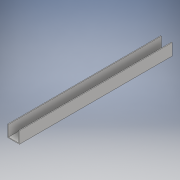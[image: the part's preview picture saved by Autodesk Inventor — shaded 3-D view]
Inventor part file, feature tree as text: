
AUTODESK INVENTOR PART (.ipt)
format: ipt  version: 2017 (Build 210142000, 142)  size: 100,352 bytes
history: native  units: in
note: dims shown in document units (in); Inventor stores cm internally (conversion verified against a paired STEP export)
features: sketch x2, extrude x1
ambient origin geometry x8: Origin, YZ Plane, XZ Plane, XY Plane, X Axis, Y Axis, Z Axis, Center Point
bodies: Solid1 (feature_tree)
feature tree (3):
  sketch  "Sketch1"  dims[d2=0.079in d3=1.26in]
  sketch  "Sketch2"  dims[d5=16.49in d6=0.0in]
  extrude  "Extrusion1"  Depth=1.26in
